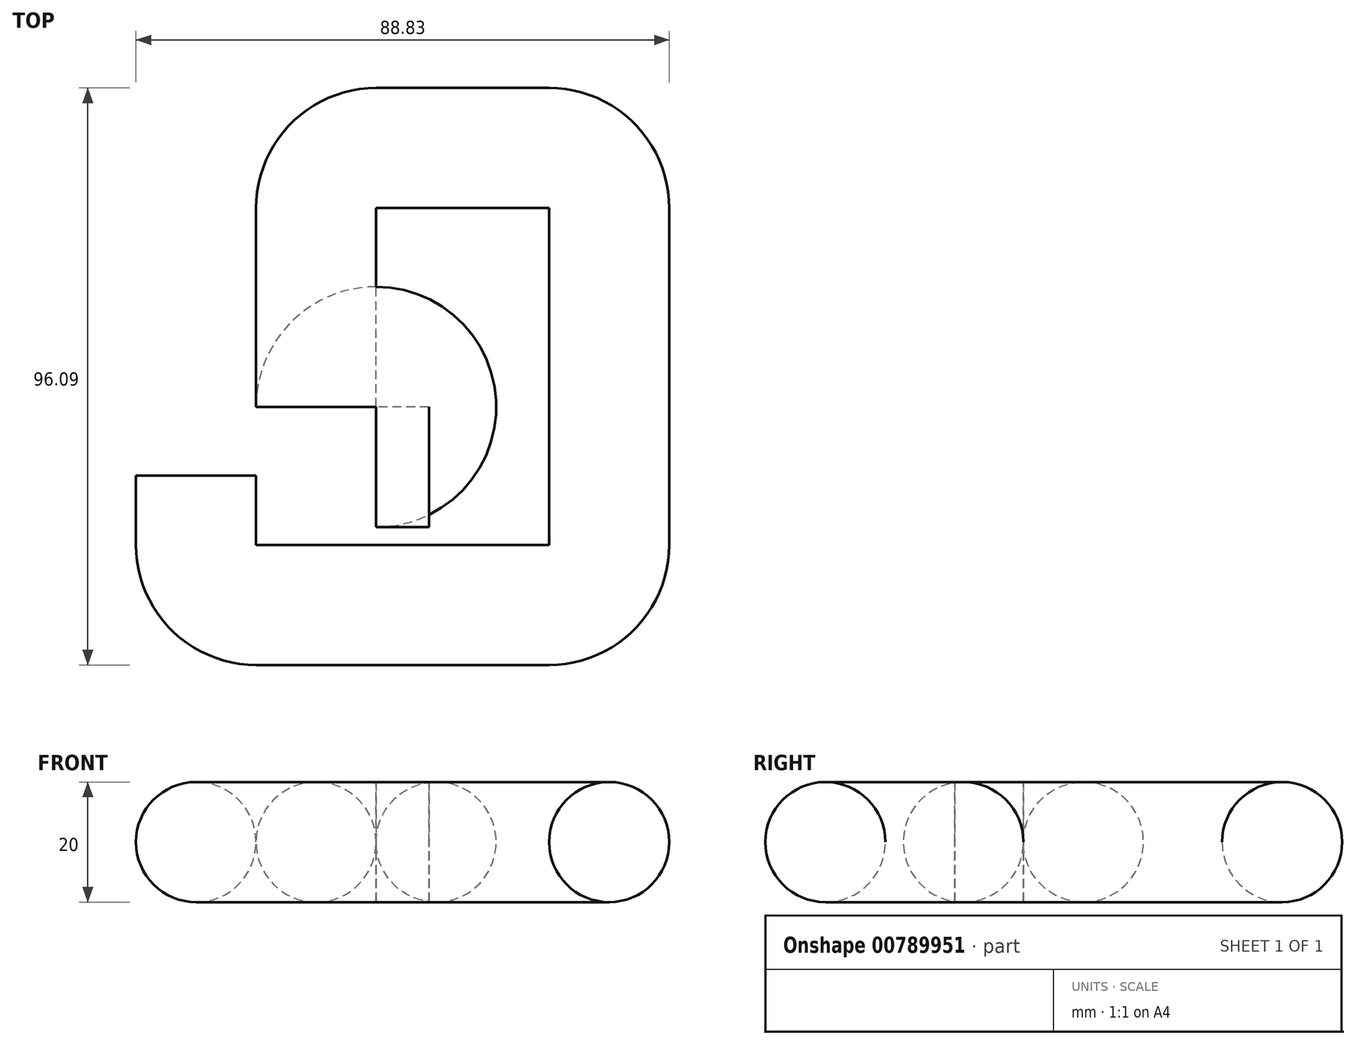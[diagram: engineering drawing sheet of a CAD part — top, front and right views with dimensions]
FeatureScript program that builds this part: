
annotation { "Feature Type Name" : "Feature", "Feature Type Description" : "" }
export const myFeature = defineFeature(function(context is Context, id is Id, definition is map)
    precondition{}
    {
        {
            var Q0;
            Q0=qCreatedBy(makeId("Top.planeOp"),FACE);
            var sketch = newSketch(context, id + "F0", { "sketchPlane" : qUnion([Q0])});
            skLineSegment(sketch, "E0", {"start": v(0, 0) * mm, "end": v(-8.8, 0) * mm});
            skLineSegment(sketch, "E1", {"start": v(-18.8, 10) * mm, "end": v(-18.8, 43.1) * mm});
            skLineSegment(sketch, "E2", {"start": v(-8.8, 53.1) * mm, "end": v(20.02, 53.1) * mm});
            skLineSegment(sketch, "E3", {"start": v(30.02, 43.1) * mm, "end": v(30.02, -12.98) * mm});
            skPoint(sketch, "E4.visualSharp", {"position": v(-18.8, 53.1) * mm});
            skArc(sketch, "E4.filletArc", {"start": v(-8.8, 53.1) * mm, "mid": v(-15.87, 50.18) * mm, "end": v(-18.8, 43.1) * mm});
            skPoint(sketch, "E5.visualSharp", {"position": v(-18.8, 0) * mm});
            skArc(sketch, "E5.filletArc", {"start": v(-18.8, 10) * mm, "mid": v(-15.87, 2.93) * mm, "end": v(-8.8, 0) * mm});
            skPoint(sketch, "E6.visualSharp", {"position": v(30.02, 53.1) * mm});
            skArc(sketch, "E6.filletArc", {"start": v(30.02, 43.1) * mm, "mid": v(27.09, 50.18) * mm, "end": v(20.02, 53.1) * mm});
            skPoint(sketch, "E7.visualSharp", {"position": v(30.02, -22.98) * mm});
            skArc(sketch, "E7.filletArc", {"start": v(20.02, -22.98) * mm, "mid": v(27.09, -20.05) * mm, "end": v(30.02, -12.98) * mm});
            skLineSegment(sketch, "E8", {"start": v(-38.8, -12.98) * mm, "end": v(-38.8, -1.46) * mm});
            skPoint(sketch, "E9.visualSharp", {"position": v(-38.8, -22.98) * mm});
            skArc(sketch, "E9.filletArc", {"start": v(-38.8, -12.98) * mm, "mid": v(-35.88, -20.05) * mm, "end": v(-28.8, -22.98) * mm});
            skLineSegment(sketch, "E10", {"start": v(-28.8, -22.98) * mm, "end": v(20.02, -22.98) * mm});
            skSolve(sketch);
        }
        {
            var Q0;
            Q0=qCreatedBy(makeId("Right.planeOp"),FACE);
            var sketch = newSketch(context, id + "F1", { "sketchPlane" : qUnion([Q0])});
            skCircle(sketch, "E11", {"center": v(0, 0) * mm, "radius": 10 * mm});
            skSolve(sketch);
        }
        {
            var Q0;
            Q0 = qSketchRegion(id + "F1", true);
            var Q1;
            Q1 = qConstructionFilter(qBodyType(qCreatedBy(id + "F0" ,EDGE), BodyType.WIRE), ConstructionObject.NO);
            sweep(context, id + "F2", {"profiles" : qUnion([Q0]), "path" : qUnion([Q1])});
        }
    });
